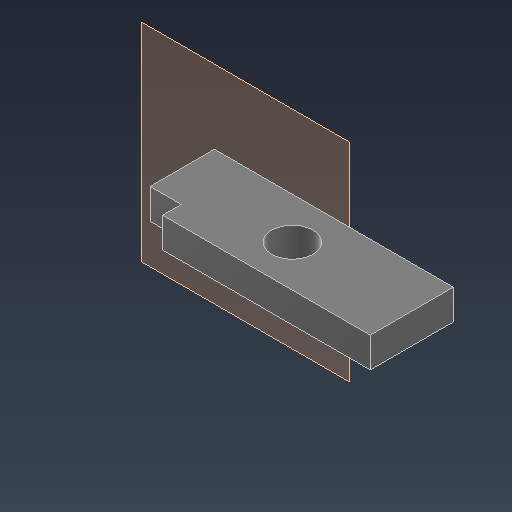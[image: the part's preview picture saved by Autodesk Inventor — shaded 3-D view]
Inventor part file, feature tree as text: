
AUTODESK INVENTOR PART (.ipt)
format: ipt  version: 2021.3 (Build 253353000, 353)  size: 105,984 bytes
history: native  units: mm
features: sketch x3, extrude x3, plane x1
ambient origin geometry x8: Origin, YZ Plane, XZ Plane, XY Plane, X Axis, Y Axis, Z Axis, Center Point
bodies: Solid1 (feature_tree)
feature tree (7):
  plane  "Work Plane1"
  sketch  "Sketch1"  dims[d0=5.0mm d1=2.9mm d2=20.0mm d4=0.0mm d5=8.0mm]
  sketch  "Sketch2"  dims[d6=6.2mm d8=0.0mm d9=3.0mm d10=4.0mm d11=8.5mm d13=0.0mm d14=0.0mm]
  sketch  "Sketch3"
  extrude  "Extrusion1"  Depth=2.9mm TaperAngle=0.0deg
  extrude  "Extrusion2"  Depth=3.0mm TaperAngle=0.0deg
  extrude  "Extrusion3"  [1 undecoded]
note: 1 required parameter value undecoded (feature->parameter linkage not recoverable at this tier; creation-order binding heuristic only, values carry confidence <= 0.55)
